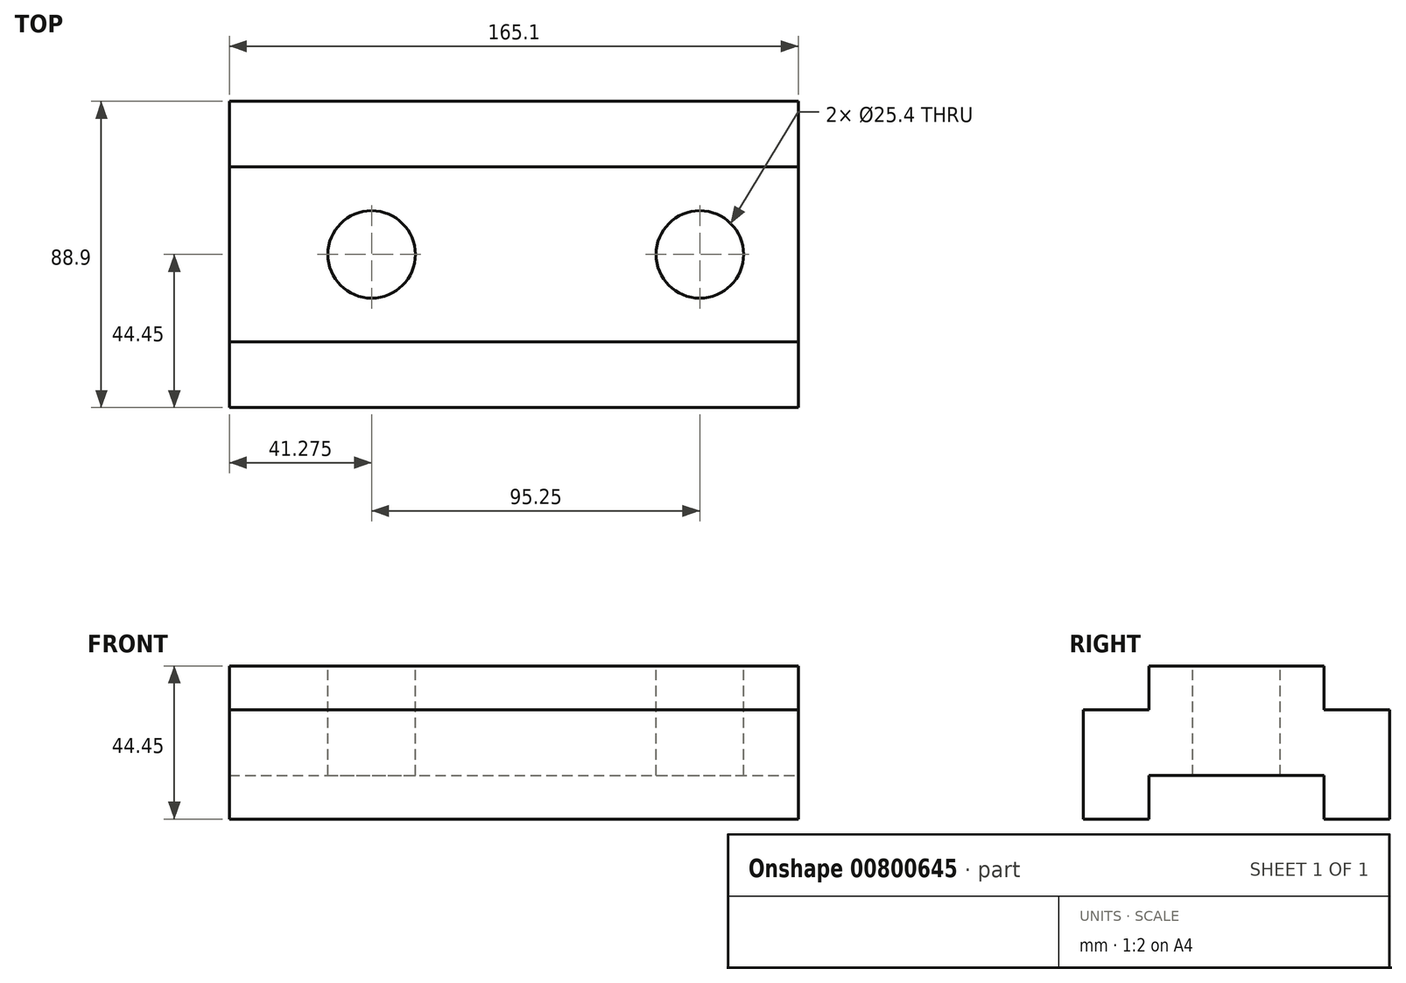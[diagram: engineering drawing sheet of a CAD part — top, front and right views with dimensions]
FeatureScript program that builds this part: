
annotation { "Feature Type Name" : "Feature", "Feature Type Description" : "" }
export const myFeature = defineFeature(function(context is Context, id is Id, definition is map)
    precondition{}
    {
        {
            var Q0;
            Q0=qCreatedBy(makeId("Front.planeOp"),FACE);
            var sketch = newSketch(context, id + "F0", { "sketchPlane" : qUnion([Q0])});
            skLineSegment(sketch, "E0", {"start": v(0, 0) * mm, "end": v(165.1, 0) * mm});
            skLineSegment(sketch, "E1", {"start": v(165.1, 0) * mm, "end": v(165.1, 44.45) * mm});
            skLineSegment(sketch, "E2", {"start": v(165.1, 44.45) * mm, "end": v(0, 44.45) * mm});
            skLineSegment(sketch, "E3", {"start": v(0, 44.45) * mm, "end": v(0, 0) * mm});
            skSolve(sketch);
        }
        {
            var Q0;
            Q0=makeQuery(id+"F0.imprint","IMPRINT",FACE,{"disambiguationData":[TD([[makeQuery(id+"F0.imprint","IMPRINT",EDGE,{"derivedFrom":sQuery(id+"F0.wireOp",EDGE,"E0")}),1.0]])]});
            extrude(context, id + "F1", {"entities" : qUnion([Q0]), "depth" : 88.9 * mm, "offsetDistance" : 25.4 * mm});
        }
        {
            var Q0;
            Q0=makeQuery(id+"F1.opExtrude","SWEPT_FACE",FACE,{"disambiguationData":[OSD([sQuery(id+"F0.wireOp",EDGE,"E2")])]});
            var sketch = newSketch(context, id + "F2", { "sketchPlane" : qUnion([Q0])});
            skLineSegment(sketch, "E4", {"start": v(0, -69.85) * mm, "end": v(0, -88.9) * mm});
            skLineSegment(sketch, "E5", {"start": v(0, -69.85) * mm, "end": v(165.1, -69.85) * mm});
            skLineSegment(sketch, "E6", {"start": v(0, 0) * mm, "end": v(0, -19.05) * mm});
            skLineSegment(sketch, "E7", {"start": v(0, -19.05) * mm, "end": v(165.1, -19.05) * mm});
            skSolve(sketch);
        }
        {
            var Q0;
            Q0=makeQuery(id+"F2.imprint","IMPRINT",FACE,{"disambiguationData":[TD([[makeQuery(id+"F2.imprint","IMPRINT",EDGE,{"derivedFrom":sQuery(id+"F2.wireOp",EDGE,"E6")}),-1.0]])]});
            var Q1;
            Q1=makeQuery(id+"F2.imprint","IMPRINT",FACE,{"disambiguationData":[TD([[makeQuery(id+"F2.imprint","IMPRINT",EDGE,{"derivedFrom":sQuery(id+"F2.wireOp",EDGE,"E4")}),-1.0]])]});
            extrude(context, id + "F3", {"entities" : qUnion([Q0, Q1]), "operationType" : NewBodyOperationType.REMOVE, "oppositeDirection" : true, "depth" : 12.7 * mm, "offsetDistance" : 25.4 * mm});
        }
        {
            var Q0;
            Q0=makeQuery(id+"F1.opExtrude","SWEPT_FACE",FACE,{"disambiguationData":[OSD([sQuery(id+"F0.wireOp",EDGE,"E1")])]});
            var sketch = newSketch(context, id + "F4", { "sketchPlane" : qUnion([Q0])});
            skLineSegment(sketch, "E8", {"start": v(-88.9, 0) * mm, "end": v(-69.85, 0) * mm});
            skLineSegment(sketch, "E9", {"start": v(-69.85, 0) * mm, "end": v(-69.85, 12.7) * mm});
            skLineSegment(sketch, "E10", {"start": v(0, 0) * mm, "end": v(-19.05, 0) * mm});
            skLineSegment(sketch, "E11", {"start": v(-19.05, 0) * mm, "end": v(-19.05, 12.7) * mm});
            skLineSegment(sketch, "E12", {"start": v(-69.85, 12.7) * mm, "end": v(-19.05, 12.7) * mm});
            skSolve(sketch);
        }
        {
            var Q0;
            {var subQ0=sQuery(id+"F4.wireOp",EDGE,"E9");Q0=makeQuery(id+"F4.imprint","IMPRINT",FACE,{"disambiguationData":[TD([[makeQuery(id+"F4.imprint","IMPRINT",EDGE,{"derivedFrom":subQ0}),-1.0]])]});}
            extrude(context, id + "F5", {"entities" : qUnion([Q0]), "operationType" : NewBodyOperationType.REMOVE, "endBound" : BoundingType.THROUGH_ALL, "oppositeDirection" : true, "depth" : 25.4 * mm, "offsetDistance" : 25.4 * mm});
        }
        {
            var Q0;
            Q0=makeQuery(id+"F1.opExtrude","SWEPT_FACE",FACE,{"disambiguationData":[OSD([sQuery(id+"F0.wireOp",EDGE,"E2")])]});
            var sketch = newSketch(context, id + "F6", { "sketchPlane" : qUnion([Q0])});
            skLineSegment(sketch, "E13", {"start": v(0, -44.45) * mm, "end": v(41.28, -44.45) * mm, "construction": true});
            skLineSegment(sketch, "E14", {"start": v(41.28, -44.45) * mm, "end": v(136.53, -44.45) * mm, "construction": true});
            skCircle(sketch, "E15", {"center": v(41.28, -44.45) * mm, "radius": 12.7 * mm});
            skCircle(sketch, "E16", {"center": v(136.53, -44.45) * mm, "radius": 12.7 * mm});
            skSolve(sketch);
        }
        {
            var Q0;
            Q0=makeQuery(id+"F6.imprint","IMPRINT",FACE,{"disambiguationData":[TD([[makeQuery(id+"F6.imprint","IMPRINT",EDGE,{"derivedFrom":sQuery(id+"F6.wireOp",EDGE,"E15")}),1.0]])]});
            var Q1;
            Q1=makeQuery(id+"F6.imprint","IMPRINT",FACE,{"disambiguationData":[TD([[makeQuery(id+"F6.imprint","IMPRINT",EDGE,{"derivedFrom":sQuery(id+"F6.wireOp",EDGE,"E16")}),1.0]])]});
            extrude(context, id + "F7", {"entities" : qUnion([Q0, Q1]), "operationType" : NewBodyOperationType.REMOVE, "endBound" : BoundingType.THROUGH_ALL, "oppositeDirection" : true, "depth" : 25.4 * mm, "offsetDistance" : 25.4 * mm});
        }
    });
